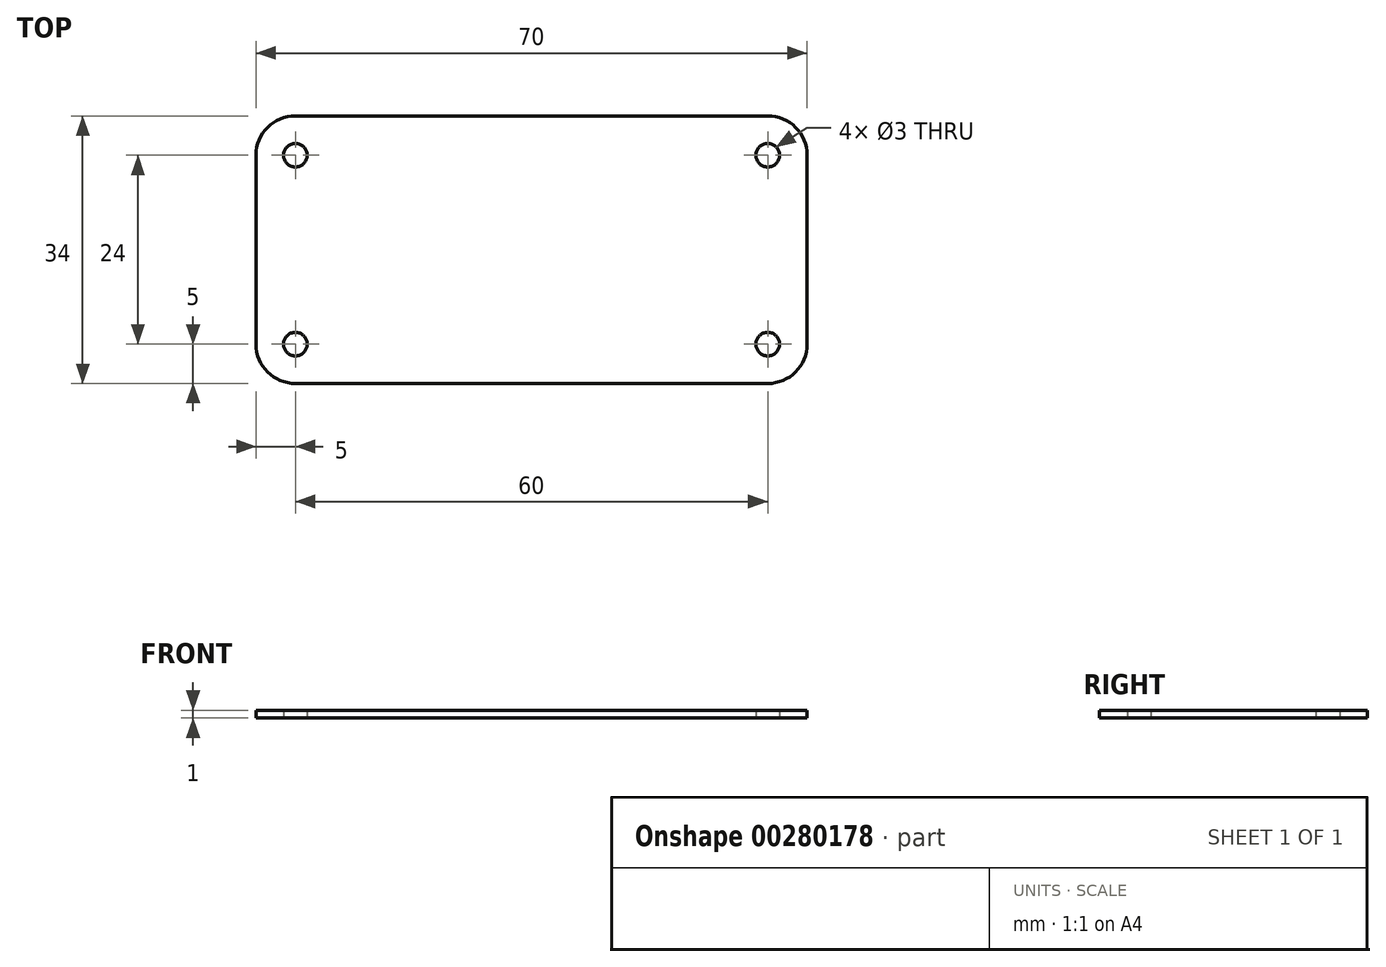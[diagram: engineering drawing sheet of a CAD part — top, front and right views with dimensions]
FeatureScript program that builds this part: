
annotation { "Feature Type Name" : "Feature", "Feature Type Description" : "" }
export const myFeature = defineFeature(function(context is Context, id is Id, definition is map)
    precondition{}
    {
        {
            var Q0;
            Q0=qCreatedBy(makeId("Top.planeOp"),FACE);
            var sketch = newSketch(context, id + "F0", { "sketchPlane" : qUnion([Q0])});
            skLineSegment(sketch, "E0.bottom", {"start": v(35, 17) * mm, "end": v(-35, 17) * mm});
            skLineSegment(sketch, "E0.top", {"start": v(35, -17) * mm, "end": v(-35, -17) * mm});
            skLineSegment(sketch, "E0.left", {"start": v(35, 17) * mm, "end": v(35, -17) * mm});
            skLineSegment(sketch, "E0.right", {"start": v(-35, 17) * mm, "end": v(-35, -17) * mm});
            skPoint(sketch, "E0.middle", {"position": v(0, 0) * mm});
            skLineSegment(sketch, "E1.bottom", {"start": v(30, 12) * mm, "end": v(-30, 12) * mm});
            skLineSegment(sketch, "E1.top", {"start": v(30, -12) * mm, "end": v(-30, -12) * mm});
            skLineSegment(sketch, "E1.left", {"start": v(30, 12) * mm, "end": v(30, -12) * mm});
            skLineSegment(sketch, "E1.right", {"start": v(-30, 12) * mm, "end": v(-30, -12) * mm});
            skCircle(sketch, "E2", {"center": v(-30, 12) * mm, "radius": 1.5 * mm});
            skCircle(sketch, "E3", {"center": v(30, 12) * mm, "radius": 1.5 * mm});
            skCircle(sketch, "E4", {"center": v(30, -12) * mm, "radius": 1.5 * mm});
            skCircle(sketch, "E5", {"center": v(-30, -12) * mm, "radius": 1.5 * mm});
            skSolve(sketch);
        }
        {
            var Q0;
            {var subQ5=sQuery(id+"F0.wireOp",EDGE,"E3");var subQ6=sQuery(id+"F0.wireOp",EDGE,"E1.bottom");var subQ7=makeQuery(id+"F0.imprint","INTERSECT",VERTEX,{"derivedFrom":[subQ6,subQ5]});Q0=makeQuery(id+"F0.imprint","IMPRINT",FACE,{"disambiguationData":[TD([[makeQuery(id+"F0.imprint","IMPRINT",EDGE,{"disambiguationData":[TD([[subQ7,-1.0]])],"derivedFrom":subQ6}),1.0]])]});}
            var Q1;
            Q1=makeQuery(id+"F0.imprint","IMPRINT",FACE,{"disambiguationData":[TD([[makeQuery(id+"F0.imprint","IMPRINT",EDGE,{"derivedFrom":sQuery(id+"F0.wireOp",EDGE,"E0.bottom")}),1.0]])]});
            extrude(context, id + "F1", {"entities" : qUnion([Q0, Q1]), "depth" : 1 * mm});
        }
        {
            var Q0;
            Q0=makeQuery(id+"F1.opExtrude","SWEPT_EDGE",EDGE,{"disambiguationData":[OSD([sQuery(id+"F0.wireOp",EDGE,"E0.top"),sQuery(id+"F0.wireOp",EDGE,"E0.right")])]});
            var Q1;
            Q1=makeQuery(id+"F1.opExtrude","SWEPT_EDGE",EDGE,{"disambiguationData":[OSD([sQuery(id+"F0.wireOp",EDGE,"E0.bottom"),sQuery(id+"F0.wireOp",EDGE,"E0.right")])]});
            var Q2;
            Q2=makeQuery(id+"F1.opExtrude","SWEPT_EDGE",EDGE,{"disambiguationData":[OSD([sQuery(id+"F0.wireOp",EDGE,"E0.bottom"),sQuery(id+"F0.wireOp",EDGE,"E0.left")])]});
            var Q3;
            Q3=makeQuery(id+"F1.opExtrude","SWEPT_EDGE",EDGE,{"disambiguationData":[OSD([sQuery(id+"F0.wireOp",EDGE,"E0.top"),sQuery(id+"F0.wireOp",EDGE,"E0.left")])]});
            fillet(context, id + "F2", {"entities" : qUnion([Q0, Q1, Q2, Q3]), "radius" : 5 * mm, "tangentPropagation" : true, "allowEdgeOverflow" : false});
        }
    });
